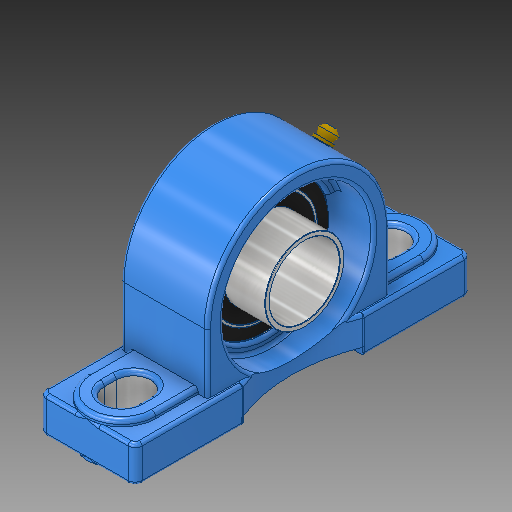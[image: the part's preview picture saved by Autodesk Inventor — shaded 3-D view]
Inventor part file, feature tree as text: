
AUTODESK INVENTOR PART (.ipt)
format: ipt  version: 2019 (Build 230136000, 136)  size: 797,184 bytes
history: native  units: mm
features: sketch x28, extrude x23, fillet x14, plane x8, mirror x6, revolve x1
ambient origin geometry x8: Origin, YZ Plane, XZ Plane, XY Plane, X Axis, Y Axis, Z Axis, Center Point
bodies: Solid1 (feature_tree)
feature tree (80):
  extrude  "Extrusion1"  Depth=167.0mm
  fillet  "Fillet1"  Radius=23.8mm
  plane  "Work Plane1"
  extrude  "Extrusion2"  Depth=18.0mm TaperAngle=0.0deg
  sketch  "Sketch3"  dims[d6=3.5mm d10=43.0mm d11=0.0mm]
  extrude  "Extrusion3"  Depth=43.0mm TaperAngle=0.0deg
  sketch  "Sketch4"  dims[d14=3.0mm d15=0.0mm d18=3.0mm d19=0.0mm]
  extrude  "Extrusion4"  Depth=3.0mm TaperAngle=0.0deg
  plane  "Work Plane2"
  mirror  "Mirror1"
  extrude  "Extrusion5"  Depth=74.25mm
  sketch  "Sketch7"  dims[d29=65.0mm d30=18.0mm d31=0.0mm]
  extrude  "Extrusion6"  Depth=18.0mm TaperAngle=0.0deg
  extrude  "Extrusion7"  Depth=18.0mm TaperAngle=0.0deg
  extrude  "Extrusion8"  Depth=1.58mm
  extrude  "Extrusion9"  Depth=1.58mm
  plane  "Work Plane4"
  mirror  "Mirror3"
  fillet  "Fillet2"  Radius=1.58mm
  fillet  "Fillet3"  Radius=1.58mm
  fillet  "Fillet4"  Radius=1.58mm
  fillet  "Fillet5"  [1 undecoded]
  plane  "Work Plane5"
  mirror  "Mirror4"
  fillet  "Fillet6"  Radius=65.0mm
  fillet  "Fillet7"  Radius=54.0mm
  plane  "Work Plane6"
  revolve  "Revolution1"  [1 undecoded]
  sketch  "Sketch14"  dims[d73=12.8mm d74=0.0mm d75=12.8mm d76=0.0mm]
  sketch  "Sketch15"  dims[d77=0.2mm d78=0.2mm]
  plane  "Work Plane7"
  extrude  "Extrusion10"  Depth=52.0mm
  plane  "Work Plane8"
  extrude  "Extrusion11"  Depth=12.8mm TaperAngle=0.0deg
  extrude  "Extrusion12"  Depth=0.2mm
  extrude  "Extrusion13"  Depth=42.9mm TaperAngle=0.0deg
  fillet  "Fillet8"  Radius=0.2mm
  fillet  "Fillet9"  Radius=0.2mm
  fillet  "Fillet10"  Radius=4.0mm
  extrude  "Extrusion14"  Depth=18.0mm TaperAngle=0.0deg
  fillet  "Fillet11"  Radius=63.5mm
  fillet  "Fillet12"  Radius=3.0mm
  extrude  "Extrusion15"  Depth=18.0mm TaperAngle=0.0deg
  sketch  "Sketch23"  dims[d105=3.0mm d106=17.0mm]
  sketch  "Sketch24"  dims[d107=21.0mm d108=0.0mm d109=2.0mm]
  extrude  "Extrusion16"  Depth=3.0mm TaperAngle=0.0deg
  sketch  "Sketch25"
  extrude  "Extrusion17"  Depth=2.0mm TaperAngle=0.0deg
  sketch  "Sketch26"
  extrude  "Extrusion18"  Depth=18.0mm
  extrude  "Extrusion19"  Depth=17.0mm
  extrude  "Extrusion20"  Depth=2.0mm
  fillet  "Fillet13"  [1 undecoded]
  plane  "Work Plane9"
  extrude  "Extrusion21"  [1 undecoded]
  extrude  "Extrusion22"  [1 undecoded]
  mirror  "Mirror5"
  mirror  "Mirror6"
  mirror  "Mirror7"
  extrude  "Extrusion23"  [1 undecoded]
  fillet  "Fillet14"  [1 undecoded]
  sketch  "Sketch1"  dims[d0=47.6mm d1=167.0mm d2=23.8mm]
  sketch  "Sketch2"  dims[d3=83.5mm d4=18.0mm d5=0.0mm]
  sketch  "Sketch5"  dims[d20=17.78mm d21=0.0mm d22=74.25mm]
  sketch  "Sketch6"  dims[d23=12.7mm d24=0.0mm d27=18.0mm d28=0.0mm]
  sketch  "Sketch8"  dims[d34=8.0mm d35=0.0mm d36=1.58mm]
  sketch  "Sketch9"  dims[d37=1.58mm d38=1.58mm d39=1.58mm d40=1.58mm d41=1.58mm d56=90.0deg]
  sketch  "Sketch10"  dims[d62=24.5mm d63=18.4mm d64=0.0mm d65=0.0mm d66=65.0mm d67=54.0mm]
  sketch  "Sketch11"  dims[d68=52.0mm d69=13.0mm d70=0.0mm]
  sketch  "Sketch13"  dims[d71=54.0mm d72=52.0mm]
  sketch  "Sketch17"  dims[d79=0.2mm d80=42.9mm d81=0.0mm d82=0.2mm d83=0.2mm d84=4.0mm d85=0.0mm]
  sketch  "Sketch18"  dims[d86=100.0mm d87=0.0mm d88=18.0mm d89=0.0mm d90=63.5mm d91=3.0mm]
  sketch  "Sketch19"  dims[d92=17.0mm d93=18.0mm d94=0.0mm]
  sketch  "Sketch20"  dims[d95=3.0mm d96=0.0mm d97=565.0mm d98=0.0mm]
  sketch  "Sketch21"  dims[d99=2.0mm d100=565.0mm d101=0.0mm]
  sketch  "Sketch22"  dims[d102=18.0mm d103=0.0mm d104=63.5mm]
  sketch  "Sketch27"
  sketch  "Sketch28"
  sketch  "Sketch29"
  sketch  "Sketch30"
note: 7 required parameter values undecoded (feature->parameter linkage not recoverable at this tier; creation-order binding heuristic only, values carry confidence <= 0.55)